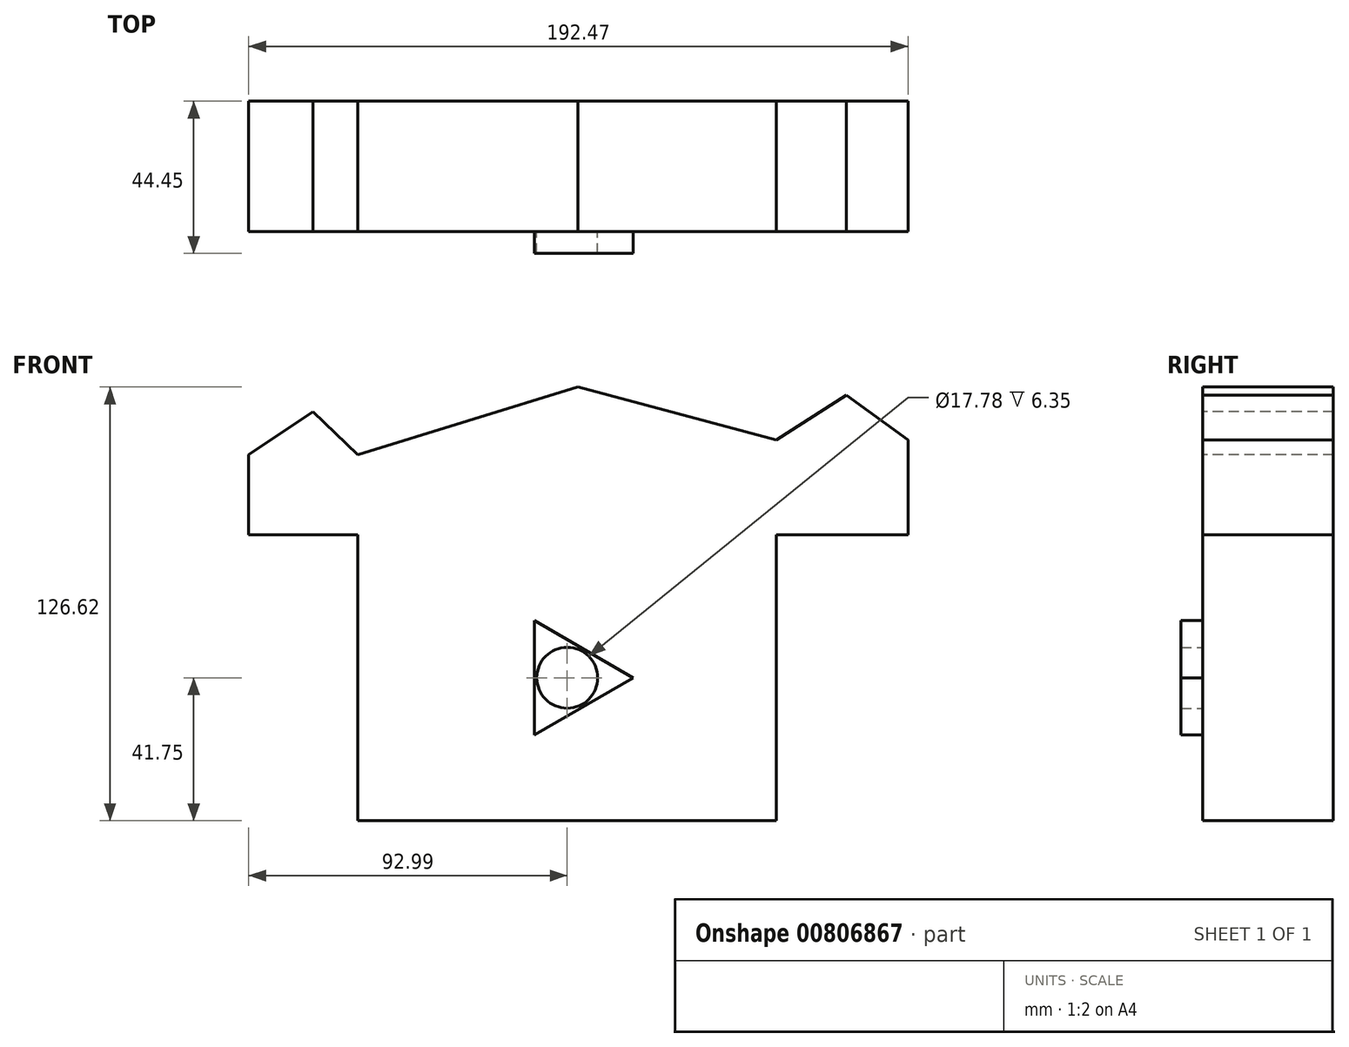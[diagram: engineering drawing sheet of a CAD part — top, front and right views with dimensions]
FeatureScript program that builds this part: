
annotation { "Feature Type Name" : "Feature", "Feature Type Description" : "" }
export const myFeature = defineFeature(function(context is Context, id is Id, definition is map)
    precondition{}
    {
        {
            var Q0;
            Q0=qCreatedBy(makeId("Front.planeOp"),FACE);
            var sketch = newSketch(context, id + "F0", { "sketchPlane" : qUnion([Q0])});
            skLineSegment(sketch, "E0.top", {"start": v(61.08, -41.75) * mm, "end": v(-61.08, -41.75) * mm});
            skLineSegment(sketch, "E0.left", {"start": v(61.08, 41.75) * mm, "end": v(61.08, -41.75) * mm});
            skLineSegment(sketch, "E0.right", {"start": v(-61.08, 41.75) * mm, "end": v(-61.08, -41.75) * mm});
            skPoint(sketch, "E0.middle", {"position": v(0, 0) * mm});
            skLineSegment(sketch, "E1.bottom", {"start": v(61.08, 41.75) * mm, "end": v(99.48, 41.75) * mm});
            skLineSegment(sketch, "E1.left", {"start": v(61.08, 41.75) * mm, "end": v(61.08, 69.4) * mm});
            skLineSegment(sketch, "E1.right", {"start": v(99.48, 41.75) * mm, "end": v(99.48, 69.4) * mm});
            skLineSegment(sketch, "E2.bottom", {"start": v(-61.08, 41.75) * mm, "end": v(-93, 41.75) * mm});
            skLineSegment(sketch, "E2.left", {"start": v(-61.08, 41.75) * mm, "end": v(-61.08, 65.1) * mm});
            skLineSegment(sketch, "E2.right", {"start": v(-93, 41.75) * mm, "end": v(-93, 65.1) * mm});
            skLineSegment(sketch, "E3", {"start": v(-61.08, 65.1) * mm, "end": v(3.11, 84.87) * mm});
            skLineSegment(sketch, "E4", {"start": v(3.11, 84.87) * mm, "end": v(61.08, 69.4) * mm});
            skLineSegment(sketch, "E5", {"start": v(61.08, 69.4) * mm, "end": v(81.52, 82.51) * mm});
            skLineSegment(sketch, "E6", {"start": v(81.52, 82.51) * mm, "end": v(99.48, 69.4) * mm});
            skLineSegment(sketch, "E7", {"start": v(-93, 65.1) * mm, "end": v(-74.2, 77.69) * mm});
            skLineSegment(sketch, "E8", {"start": v(-74.2, 77.69) * mm, "end": v(-61.08, 65.1) * mm});
            skSolve(sketch);
        }
        {
            var Q0;
            Q0 = qSketchRegion(id + "F0", true);
            extrude(context, id + "F1", {"entities" : qUnion([Q0]), "oppositeDirection" : true, "depth" : 38.1 * mm, "offsetDistance" : 25.4 * mm});
        }
        {
            var Q0;
            Q0=makeQuery(id+"F0.imprint","IMPRINT",FACE,{"disambiguationData":[TD([[makeQuery(id+"F0.imprint","IMPRINT",EDGE,{"derivedFrom":sQuery(id+"F0.wireOp",EDGE,"E0.top")}),-1.0]])]});
            var sketch = newSketch(context, id + "F2", { "sketchPlane" : qUnion([Q0])});
            skCircle(sketch, "E9.cCircle", {"center": v(0, 0) * mm, "radius": 19.27 * mm, "construction": true});
            skLineSegment(sketch, "E9.0", {"start": v(19.27, 0) * mm, "end": v(-9.64, -16.7) * mm});
            skLineSegment(sketch, "E9.1", {"start": v(-9.64, -16.7) * mm, "end": v(-9.64, 16.7) * mm});
            skLineSegment(sketch, "E9.2", {"start": v(-9.64, 16.7) * mm, "end": v(19.27, 0) * mm});
            skCircle(sketch, "E10", {"center": v(0, 0) * mm, "radius": 8.9 * mm});
            skSolve(sketch);
        }
        {
            var Q0;
            Q0 = qSketchRegion(id + "F2", true);
            extrude(context, id + "F3", {"entities" : qUnion([Q0]), "operationType" : NewBodyOperationType.ADD, "depth" : 6.35 * mm, "offsetDistance" : 25.4 * mm});
        }
    });
